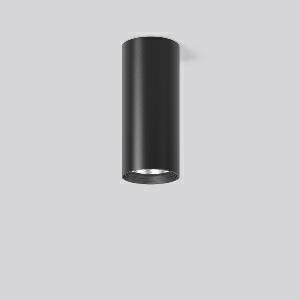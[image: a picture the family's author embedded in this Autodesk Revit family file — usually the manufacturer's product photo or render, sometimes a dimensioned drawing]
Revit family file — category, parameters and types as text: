
# Revit family: heledon_mini_a_931202_003_1_6d71
name_source: partatom
category: Lighting Fixtures
units: mm (PartAtom-declared; Revit-internal decimal feet)

## family parameters
Cut with Voids When Loaded = No
Host = Face
Light Source = No
Part Type = Normal
Room Calculation Point = No
Round Connector Dimension = Use Diameter
Shared = No

## types (1)
- HELEDON mini A (1 x LED Modul 940, 2750 lm, 4000)
    Apparent Load = 20 VA
    Approval mark = CE
    CIE Flux Codes = 95 99 100 100 100
    Color Rendering = 92
    Color Temperature = 4000
    Default Elevation = 1800 mm
    Description = Series: HELEDON mini
Cylindrical surface-mounted downlight. Housing: die-cast aluminium, powder-coated. Internal ceiling frame polycarbonate with bayonet mounting. Black plastic ring and recessed LED to prevent glare from the side. Optical assembly with reflector made of MIRO-Silver with 98% total light reflection for outstanding efficiency - can be changed without tools. Best colour rendering index Ra>90. Suitable for Ceiling mounting. Easy installation with a separate ceiling frame with bayonet mounting and plug connection. Driver integrated. Connected via plug-in connector. High quality converter without flickering and stroboscopic effect. The following accessories can be mounted without use of tools: interchangeable lenses, decorative glasses, honeycomb louvre, clear and frosted diffusers, white interchangeable plastic ring. 
Colour: deep black, matt (RAL 9005)
Diameter: 87 mm
Height: 197 mm
Lamp: LED
Socket: without socket
Colour temperature: 4000K
Colour rendering index (CRI): 92
System power: 20 W
Rated luminous flux: 2750 lm
Luminous efficiency: 138 lm/W
Control gear: Regulated power supply
Protection class: I
Type of protection: IP 20
    Height = 197 mm
    Lamp = 1 x LED Modul 940
    Lamp Light Flux = 2750 lm
    Lamp count = 1
    Length = 87 mm
    Lifetime = 50000 h
    Luminous efficacy = 138 lm/W
    Manufacturer = RZB
    ModVariant = No
    Model = 931202.003.1
    Mounting Place = Ceiling
    Mounting Type = Surface mounted
    Number of Poles = 1
    OnlyDefault = Yes
    Power Factor = 1
    Product Name = HELEDON mini A
    Product group = Surface mounted downlights
    ProductGroupID = 302
    Protection Class = Protection class I
    Protection Degree = IP 20
    RLX_Detail_Level = 1
    RLX_Emergency_Light_Flux = 0 lm
    RLX_Emergency_Type = 0
    RLX_Emergency_Type_DB = No
    RlxData = <blob elided: 109025 chars, md5=6c4c4ae1>
    Socket = socket
    Standby Power = 0 W
    System Light Flux = 2750 lm
    System Power = 20 W
    Type Comments = Product without accessories
    Type Image = 931188.003.jpg
    URL = http://relux.com
    VarID = ---
    Voltage = 230 V
    Voltage Range = 220-240 V
    Weight = 0.00 kg
    Width = 0 mm  [stored 0 ft]

note: [stored X ft] marks values corroborated as IEEE doubles in the binary element streams (Revit-internal decimal feet)

## geometry (parser evidence)
native form markers: Blend x4, Sweep x11
no freeform markers — native parametric forms only
